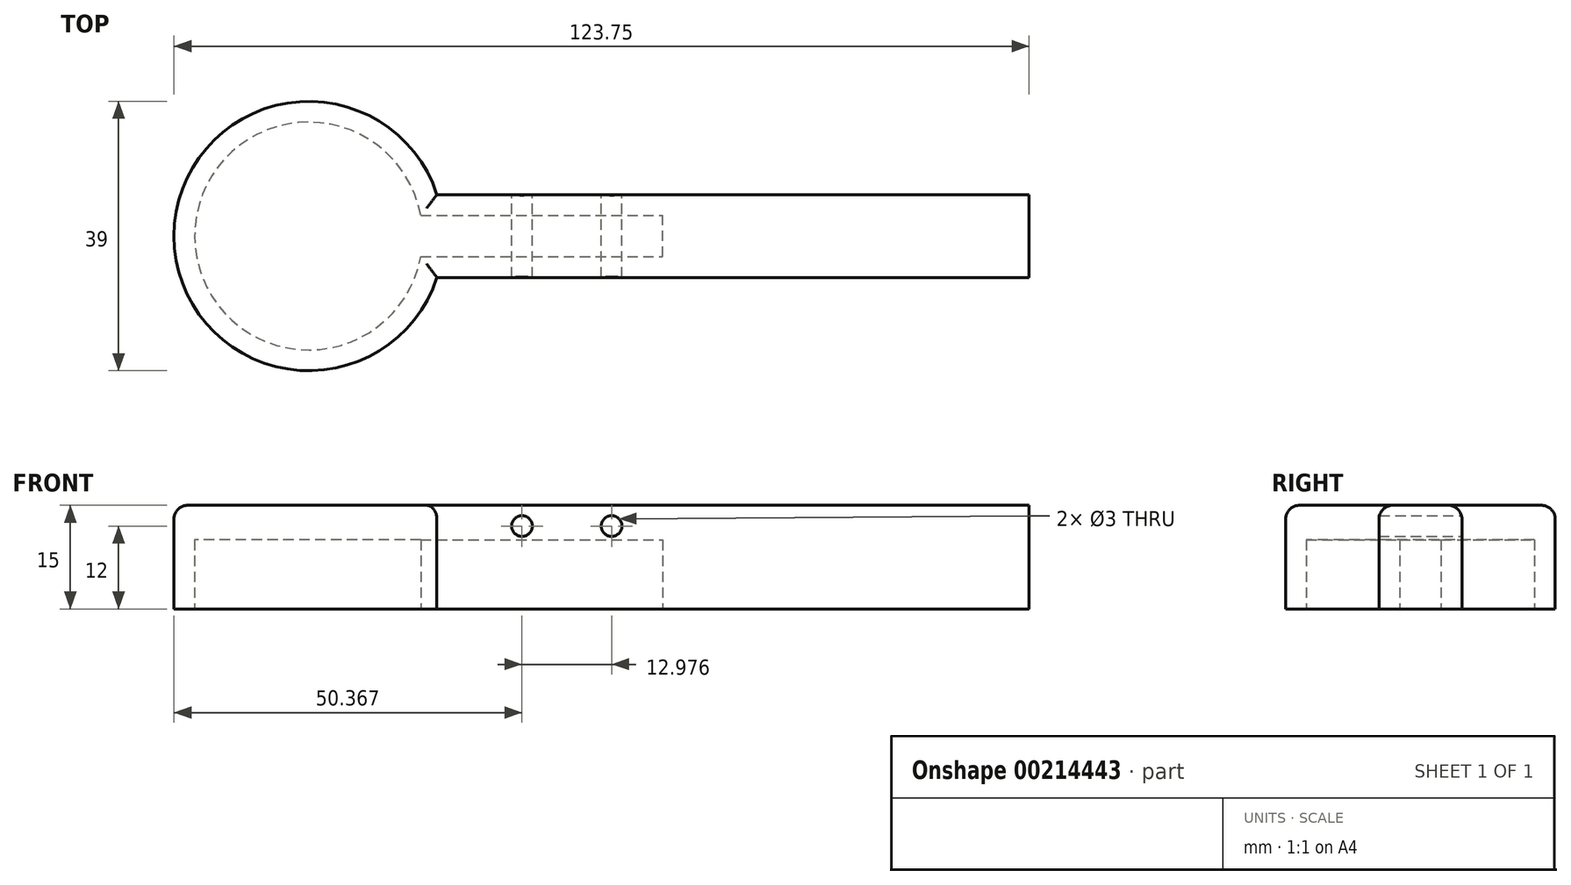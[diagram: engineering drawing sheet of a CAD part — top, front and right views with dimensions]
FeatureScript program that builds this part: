
annotation { "Feature Type Name" : "Feature", "Feature Type Description" : "" }
export const myFeature = defineFeature(function(context is Context, id is Id, definition is map)
    precondition{}
    {
        {
            var Q0;
            Q0=qCreatedBy(makeId("Top.planeOp"),FACE);
            var sketch = newSketch(context, id + "F6", { "sketchPlane" : qUnion([Q0])});
            skArc(sketch, "E0", {"start": v(-18.1, 52.18) * mm, "mid": v(-50.83, 49.18) * mm, "end": v(-18.1, 46.18) * mm});
            skLineSegment(sketch, "E1.bottom", {"start": v(-18.1, 46.18) * mm, "end": v(16.92, 46.18) * mm});
            skLineSegment(sketch, "E1.top", {"start": v(-18.1, 52.18) * mm, "end": v(16.92, 52.18) * mm});
            skLineSegment(sketch, "E1.right", {"start": v(16.92, 46.18) * mm, "end": v(16.92, 52.18) * mm});
            skLineSegment(sketch, "E2", {"start": v(16.92, 49.18) * mm, "end": v(-17.83, 49.18) * mm, "construction": true});
            skLineSegment(sketch, "E3.0", {"start": v(17.17, 46.18) * mm, "end": v(17.17, 52.18) * mm});
            skPoint(sketch, "E4.orphan", {"position": v(-22.16, 52.18) * mm});
            skPoint(sketch, "E1.left.end.orphan", {"position": v(-22.16, 49.18) * mm});
            skPoint(sketch, "E1.left.start.orphan", {"position": v(-22.16, 46.18) * mm});
            skArc(sketch, "E5.0", {"start": v(-15.16, 52.73) * mm, "mid": v(-53.83, 49.18) * mm, "end": v(-15.16, 45.63) * mm});
            skLineSegment(sketch, "E6.0", {"start": v(-18.1, 43.18) * mm, "end": v(19.92, 43.18) * mm});
            skLineSegment(sketch, "E6.1", {"start": v(19.92, 43.18) * mm, "end": v(19.92, 55.18) * mm});
            skLineSegment(sketch, "E6.2", {"start": v(-18.1, 55.18) * mm, "end": v(19.92, 55.18) * mm});
            skSolve(sketch);
        }
        {
            var Q0;
            Q0=makeQuery(id+"F6.imprint","IMPRINT",FACE,{"disambiguationData":[TD([[makeQuery(id+"F6.imprint","IMPRINT",EDGE,{"derivedFrom":sQuery(id+"F6.wireOp",EDGE,"E0")}),-1.0]])]});
            var Q1;
            Q1=makeQuery(id+"F6.imprint","IMPRINT",FACE,{"disambiguationData":[TD([[makeQuery(id+"F6.imprint","IMPRINT",EDGE,{"derivedFrom":sQuery(id+"F6.wireOp",EDGE,"E0")}),1.0]])]});
            extrude(context, id + "F0", {"entities" : qUnion([Q0, Q1]), "depth" : 15 * mm});
        }
        {
            var Q0;
            Q0=makeQuery(id+"F6.imprint","IMPRINT",FACE,{"disambiguationData":[TD([[makeQuery(id+"F6.imprint","IMPRINT",EDGE,{"derivedFrom":sQuery(id+"F6.wireOp",EDGE,"E0")}),1.0]])]});
            extrude(context, id + "F1", {"entities" : qUnion([Q0]), "operationType" : NewBodyOperationType.REMOVE, "depth" : 10 * mm});
        }
        {
            var Q0;
            Q0=makeQuery(id+"F0.opExtrude","SWEPT_FACE",FACE,{"disambiguationData":[OSD([sQuery(id+"F6.wireOp",EDGE,"E6.1")])]});
            extrude(context, id + "F2", {"entities" : qUnion([Q0]), "operationType" : NewBodyOperationType.ADD, "depth" : 50 * mm});
        }
        {
            var Q0;
            {var subQ0=sQuery(id+"F6.wireOp",EDGE,"E6.2");Q0=makeQuery(id+"F2.boolean.opBoolean","MERGE",FACE,{"derivedFrom":[makeQuery(id+"F0.opExtrude","SWEPT_FACE",FACE,{"disambiguationData":[OSD([subQ0])]}),makeQuery(id+"F2.opExtrude","SWEPT_FACE",FACE,{"disambiguationData":[OSD([sQuery(id+"F6.wireOp",EDGE,"E6.1"),subQ0])]})]});}
            var sketch = newSketch(context, id + "F3", { "sketchPlane" : qUnion([Q0])});
            skLineSegment(sketch, "E7", {"start": v(15.78, 12) * mm, "end": v(-69.92, 12) * mm, "construction": true});
            skCircle(sketch, "E8", {"center": v(-9.51, 12) * mm, "radius": 1.5 * mm});
            skCircle(sketch, "E9", {"center": v(3.46, 12) * mm, "radius": 1.5 * mm});
            skSolve(sketch);
        }
        {
            var Q0;
            Q0=makeQuery(id+"F3.imprint","IMPRINT",FACE,{"disambiguationData":[TD([[makeQuery(id+"F3.imprint","IMPRINT",EDGE,{"derivedFrom":sQuery(id+"F3.wireOp",EDGE,"E8")}),1.0]])]});
            var Q1;
            Q1=makeQuery(id+"F3.imprint","IMPRINT",FACE,{"disambiguationData":[TD([[makeQuery(id+"F3.imprint","IMPRINT",EDGE,{"derivedFrom":sQuery(id+"F3.wireOp",EDGE,"E9")}),1.0]])]});
            extrude(context, id + "F4", {"entities" : qUnion([Q0, Q1]), "operationType" : NewBodyOperationType.REMOVE, "oppositeDirection" : true, "depth" : 25 * mm});
        }
        {
            var Q0;
            {var subQ0=sQuery(id+"F6.wireOp",EDGE,"E6.2");var subQ1=sQuery(id+"F6.wireOp",EDGE,"E6.1");Q0=makeQuery(id+"F2.boolean.opBoolean","MERGE",EDGE,{"derivedFrom":[makeQuery(id+"F0.opExtrude","CAP_EDGE",EDGE,{"disambiguationData":[OSD([subQ0])],"isStart":false}),makeQuery(id+"F2.opExtrude","SWEPT_EDGE",EDGE,{"disambiguationData":[OSD([subQ1,subQ0]),TDD([makeQuery(id+"F0.opExtrude","CAP_VERTEX",VERTEX,{"disambiguationData":[OSD([subQ1,subQ0])],"isStart":false})])]})]});}
            var Q1;
            {var subQ0=sQuery(id+"F6.wireOp",EDGE,"E6.1");var subQ1=sQuery(id+"F6.wireOp",EDGE,"E6.0");Q1=makeQuery(id+"F2.boolean.opBoolean","MERGE",EDGE,{"derivedFrom":[makeQuery(id+"F0.opExtrude","CAP_EDGE",EDGE,{"disambiguationData":[OSD([subQ1])],"isStart":false}),makeQuery(id+"F2.opExtrude","SWEPT_EDGE",EDGE,{"disambiguationData":[OSD([subQ1,subQ0]),TDD([makeQuery(id+"F0.opExtrude","CAP_VERTEX",VERTEX,{"disambiguationData":[OSD([subQ1,subQ0])],"isStart":false})])]})]});}
            var Q2;
            Q2=makeQuery(id+"F0.opExtrude","CAP_EDGE",EDGE,{"disambiguationData":[OSD([sQuery(id+"F6.wireOp",EDGE,"E5.0")])],"isStart":false});
            fillet(context, id + "F5", {"entities" : qUnion([Q0, Q1, Q2]), "radius" : 2 * mm, "tangentPropagation" : true, "allowEdgeOverflow" : false});
        }
    });
